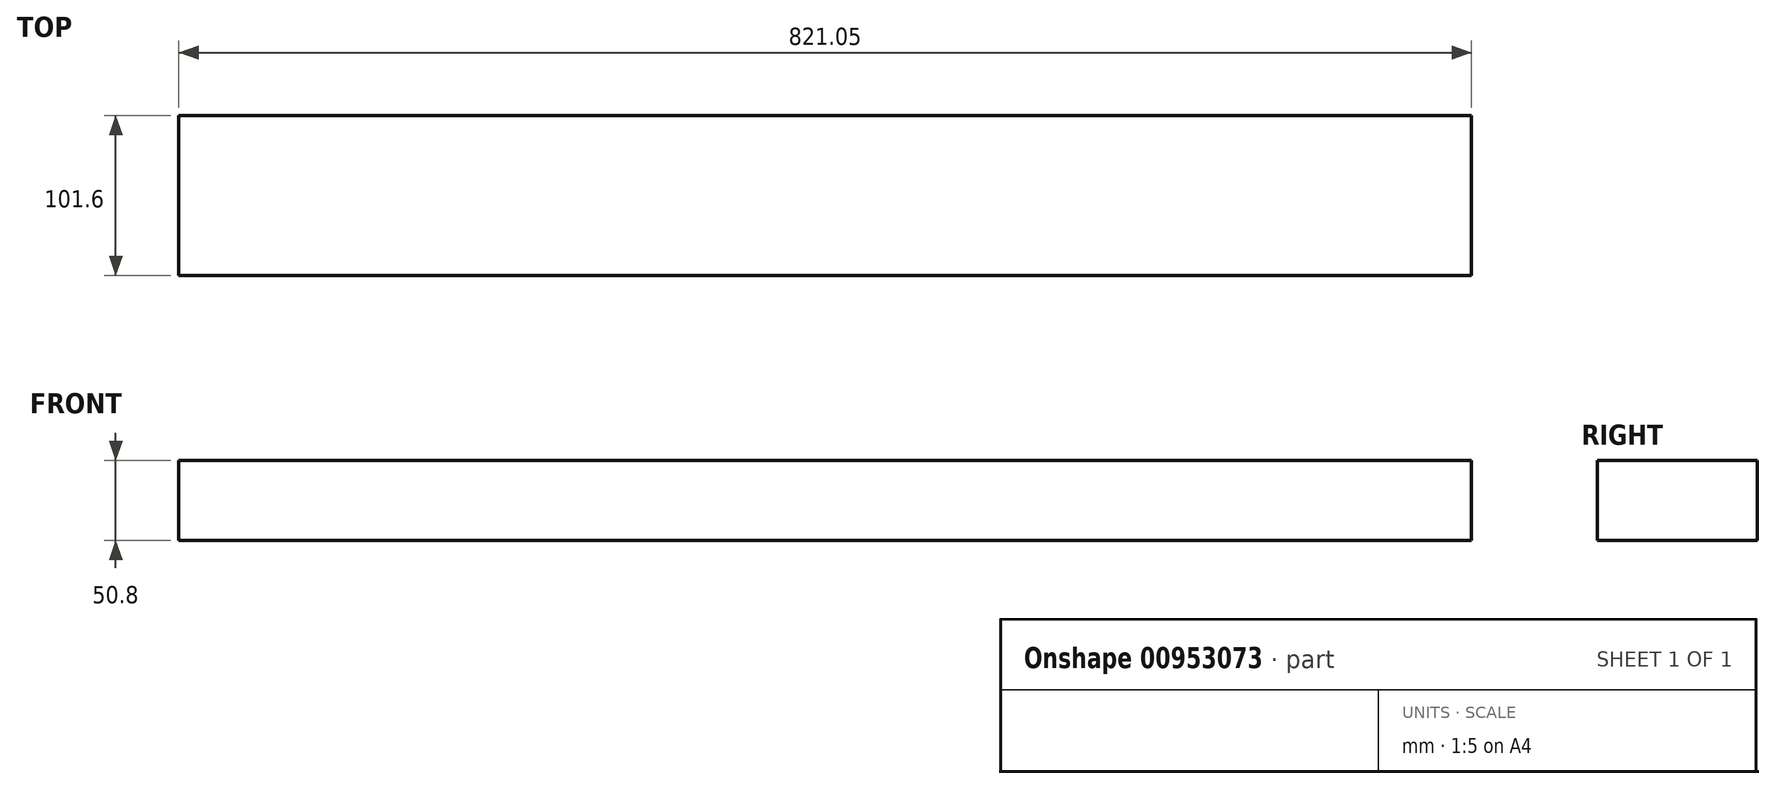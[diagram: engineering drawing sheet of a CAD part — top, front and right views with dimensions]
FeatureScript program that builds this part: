
annotation { "Feature Type Name" : "Feature", "Feature Type Description" : "" }
export const myFeature = defineFeature(function(context is Context, id is Id, definition is map)
    precondition{}
    {
        {
            var Q0;
            Q0=qCreatedBy(makeId("Top.planeOp"),FACE);
            var sketch = newSketch(context, id + "F0", { "sketchPlane" : qUnion([Q0])});
            skLineSegment(sketch, "E0", {"start": v(0, 0) * mm, "end": v(-821.06, 0) * mm});
            skLineSegment(sketch, "E1", {"start": v(-821.06, 0) * mm, "end": v(-821.06, 101.6) * mm});
            skLineSegment(sketch, "E2", {"start": v(-821.06, 101.6) * mm, "end": v(0, 101.6) * mm});
            skLineSegment(sketch, "E3", {"start": v(0, 101.6) * mm, "end": v(0, 0) * mm});
            skSolve(sketch);
        }
        {
            var Q0;
            Q0 = qSketchRegion(id + "F0", true);
            extrude(context, id + "F1", {"entities" : qUnion([Q0]), "depth" : 50.8 * mm, "offsetDistance" : 25.4 * mm});
        }
    });
